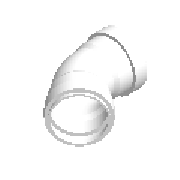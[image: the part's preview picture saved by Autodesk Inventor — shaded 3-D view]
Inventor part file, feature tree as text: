
AUTODESK INVENTOR PART (.ipt)
format: ipt  version: 2023 (Build 270158000, 158)  size: 266,240 bytes
history: native  units: mm (DEFAULTED — no unit token found)
features: other x6, sketch x3, revolve x2, sweep x1
ambient origin geometry x8: Origin, YZ Plane, XZ Plane, XY Plane, X Axis, Y Axis, Z Axis, Center Point
bodies: Solid1 (feature_tree)
feature tree (12):
  sketch  "Sketch1"  dims[d3=90.0deg d0=2.25mm]
  revolve  "Revolution1"  [1 undecoded]
  sketch  "Sketch2"  dims[d1=2.25mm d2=2.25mm]
  sweep  "Sweep1"
  revolve  "Revolution2"  [1 undecoded]
  other  "Work Point1"
  other  "Work Point2"
  other  "Work Axis31"
  other  "Work Point21"
  other  "Work Axis32"
  other  "Work Point22"
  sketch  "Sketch3"  dims[d4=2.7mm d5=2.25mm d6=6.75mm d7=40.3mm d8=18.0mm d9=18.0mm d10=0.0mm d11=6.3mm d12=40.0mm d13=3.0mm d14=2.7mm d15=45.0deg d16=17.0mm d17=17.0mm d18=40.3mm d19=2.25mm d20=2.25mm d21=2.25mm d22=2.25mm d23=4.5mm d24=2.7mm d25=3.0mm d26=40.0mm d27=6.3mm d28=18.0mm d29=18.0mm d30=45.0deg d31=17.0mm d32=17.0mm d33=2.7mm d206=90.0deg d207=0.0mm]
note: 2 required parameter values undecoded (feature->parameter linkage not recoverable at this tier; creation-order binding heuristic only, values carry confidence <= 0.55)
